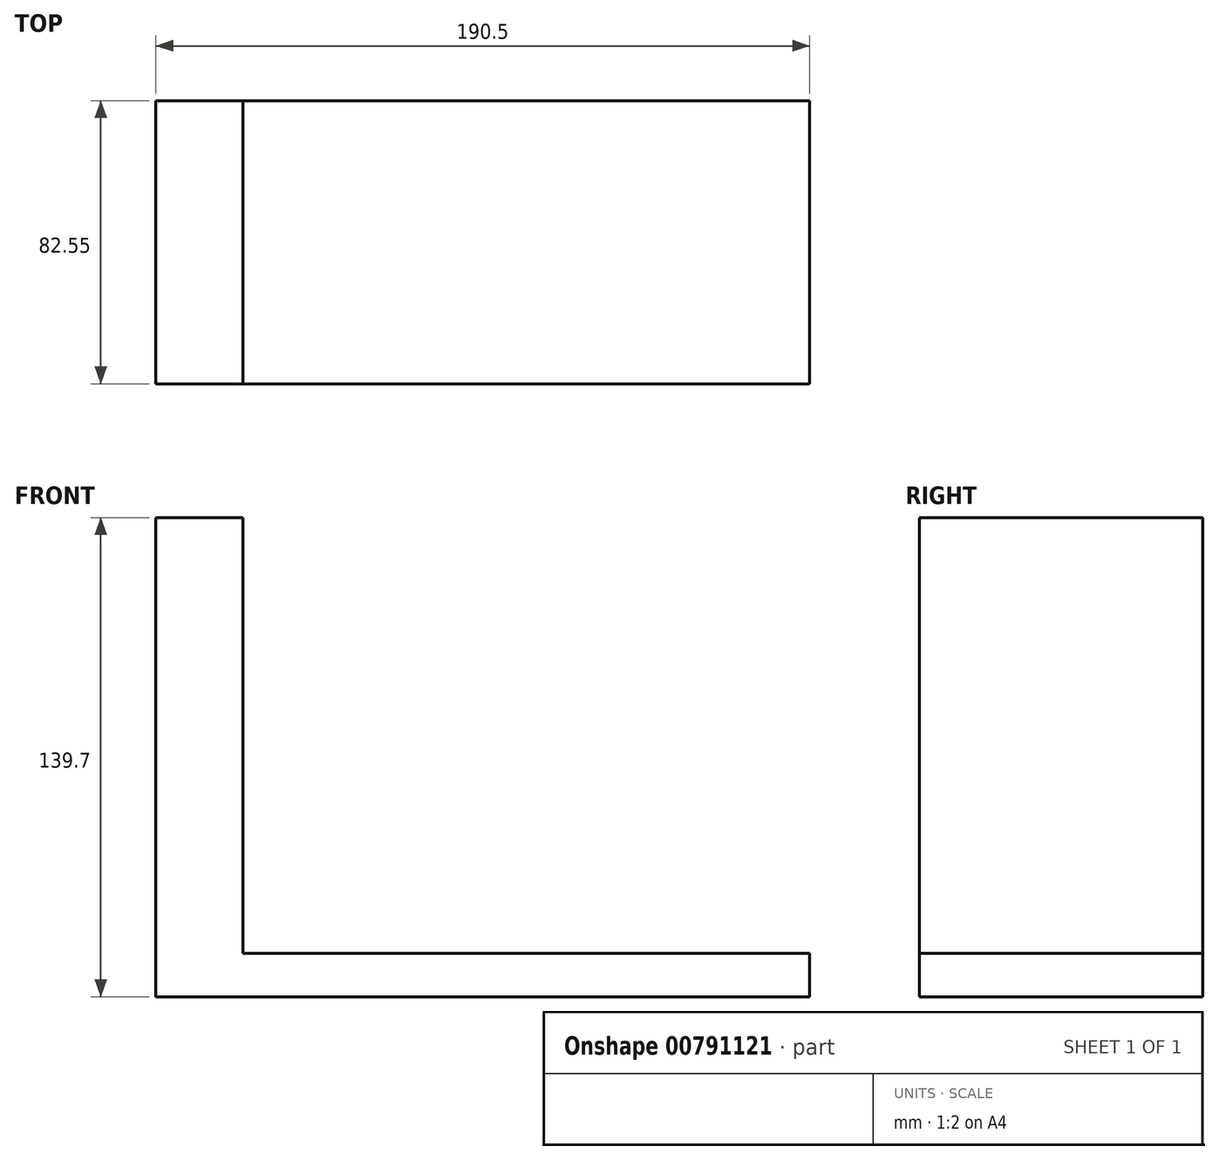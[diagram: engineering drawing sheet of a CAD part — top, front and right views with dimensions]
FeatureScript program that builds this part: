
annotation { "Feature Type Name" : "Feature", "Feature Type Description" : "" }
export const myFeature = defineFeature(function(context is Context, id is Id, definition is map)
    precondition{}
    {
        {
            var Q0;
            Q0=qCreatedBy(makeId("Front.planeOp"),FACE);
            var sketch = newSketch(context, id + "F0", { "sketchPlane" : qUnion([Q0])});
            skLineSegment(sketch, "E0", {"start": v(0, 0) * mm, "end": v(190.5, 0) * mm});
            skLineSegment(sketch, "E1", {"start": v(190.5, 0) * mm, "end": v(190.5, 12.7) * mm});
            skLineSegment(sketch, "E2", {"start": v(190.5, 12.7) * mm, "end": v(38.1, 12.7) * mm});
            skLineSegment(sketch, "E3", {"start": v(38.1, 12.7) * mm, "end": v(0, 12.7) * mm});
            skLineSegment(sketch, "E4", {"start": v(0, 12.7) * mm, "end": v(0, 0) * mm});
            skSolve(sketch);
        }
        {
            var Q0;
            Q0=makeQuery(id+"F0.imprint","IMPRINT",FACE,{"disambiguationData":[TD([[makeQuery(id+"F0.imprint","IMPRINT",EDGE,{"derivedFrom":sQuery(id+"F0.wireOp",EDGE,"E0")}),1.0]])]});
            extrude(context, id + "F1", {"entities" : qUnion([Q0]), "depth" : 82.55 * mm, "offsetDistance" : 25.4 * mm});
        }
        {
            var Q0;
            Q0=makeQuery(id+"F1.opExtrude","SWEPT_FACE",FACE,{"disambiguationData":[OSD([sQuery(id+"F0.wireOp",EDGE,"E2"),sQuery(id+"F0.wireOp",EDGE,"E3")])]});
            var sketch = newSketch(context, id + "F2", { "sketchPlane" : qUnion([Q0])});
            skLineSegment(sketch, "E5", {"start": v(0, -82.55) * mm, "end": v(25.4, -82.55) * mm, "construction": true});
            skLineSegment(sketch, "E6", {"start": v(25.4, -82.55) * mm, "end": v(25.4, 0) * mm});
            skSolve(sketch);
        }
        {
            var Q0;
            Q0 = qSketchRegion(id + "F2", true);
            var Q1;
            {var subQ0=sQuery(id+"F2.wireOp",EDGE,"E6");Q1=makeQuery(id+"F2.imprint","IMPRINT",FACE,{"disambiguationData":[TD([[makeQuery(id+"F2.imprint","IMPRINT",EDGE,{"derivedFrom":subQ0}),1.0]])]});}
            extrude(context, id + "F3", {"entities" : qUnion([Q0, Q1]), "operationType" : NewBodyOperationType.ADD, "depth" : 127 * mm, "offsetDistance" : 25.4 * mm});
        }
    });
